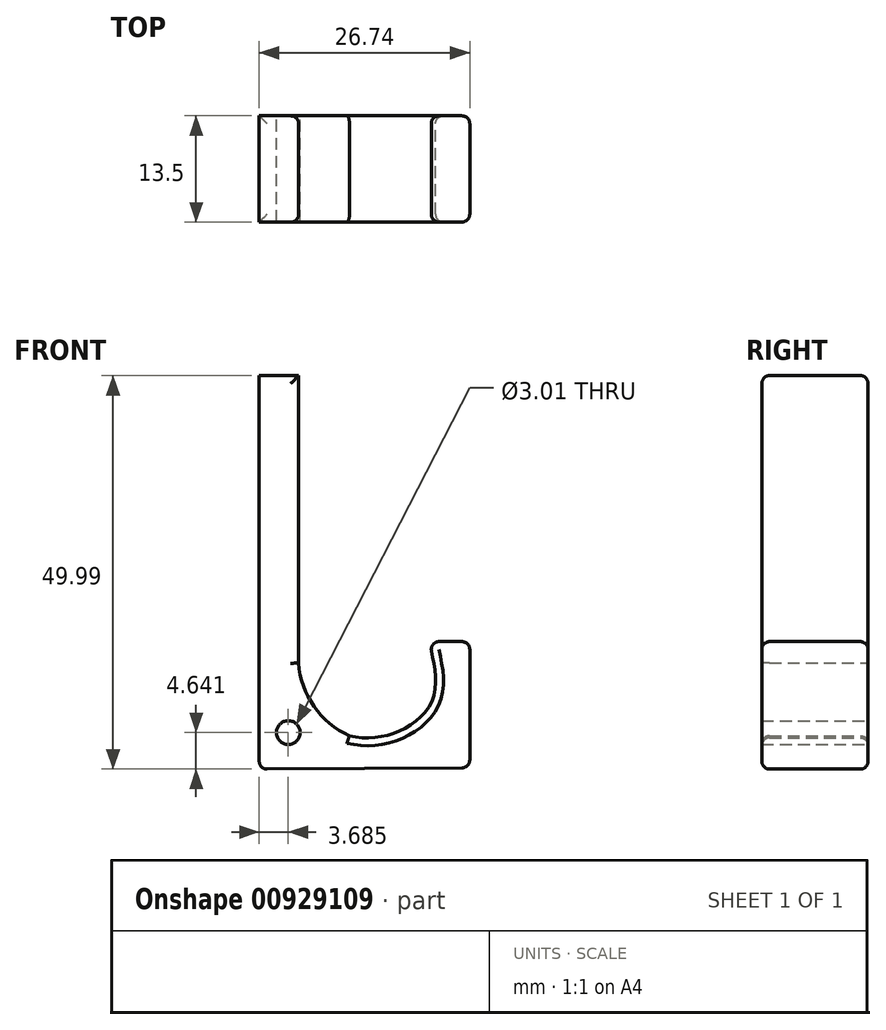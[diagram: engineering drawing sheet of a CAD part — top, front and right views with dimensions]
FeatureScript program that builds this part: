
annotation { "Feature Type Name" : "Feature", "Feature Type Description" : "" }
export const myFeature = defineFeature(function(context is Context, id is Id, definition is map)
    precondition{}
    {
        {
            var Q0;
            Q0=qCreatedBy(makeId("Front.planeOp"),FACE);
            var sketch = newSketch(context, id + "F0", { "sketchPlane" : qUnion([Q0])});
            skLineSegment(sketch, "E0", {"start": v(5.1, 13.49) * mm, "end": v(5.1, 50) * mm});
            skArc(sketch, "E1", {"start": v(5.1, 13.49) * mm, "mid": v(6.25, 9.3) * mm, "end": v(8.93, 5.9) * mm});
            skLineSegment(sketch, "E2.0", {"start": v(0.1, 0) * mm, "end": v(0.1, 50) * mm});
            skLineSegment(sketch, "E2.1", {"start": v(0.1, 0) * mm, "end": v(26.84, 0.17) * mm});
            skArc(sketch, "E3", {"start": v(5.1, 13.49) * mm, "mid": v(7.05, 7.97) * mm, "end": v(11.56, 4.24) * mm});
            skLineSegment(sketch, "E4", {"start": v(26.84, 16.2) * mm, "end": v(26.84, 0.17) * mm});
            skLineSegment(sketch, "E5", {"start": v(0.1, 50) * mm, "end": v(5.1, 50) * mm});
            skLineSegment(sketch, "E6", {"start": v(26.84, 16.2) * mm, "end": v(21.84, 16.2) * mm});
            skFitSpline(sketch, "E7", {"points": [v(21.84, 16.2) * mm, v(22.16, 8.97) * mm, v(11.56, 4.24) * mm], "startDerivative": vector(-0.62, -8.51) * mm, "endDerivative": vector(-24.07, 5.81) * mm});
            skCircle(sketch, "E8", {"center": v(3.79, 4.65) * mm, "radius": 1.5 * mm});
            skSolve(sketch);
        }
        {
            var Q0;
            {var subQ1=sQuery(id+"F0.wireOp",EDGE,"E0");Q0=makeQuery(id+"F0.imprint","IMPRINT",FACE,{"disambiguationData":[TD([[makeQuery(id+"F0.imprint","IMPRINT",EDGE,{"derivedFrom":subQ1}),1.0]])]});}
            extrude(context, id + "F1", {"entities" : qUnion([Q0]), "depth" : 13.5 * mm, "offsetDistance" : 25 * mm});
        }
        {
            var Q0;
            Q0=makeQuery(id+"F1.opExtrude","CAP_EDGE",EDGE,{"disambiguationData":[OSD([sQuery(id+"F0.wireOp",EDGE,"E7")])],"isStart":false});
            var Q1;
            Q1=makeQuery(id+"F1.opExtrude","CAP_EDGE",EDGE,{"disambiguationData":[OSD([sQuery(id+"F0.wireOp",EDGE,"E7")])],"isStart":true});
            var Q2;
            Q2=makeQuery(id+"F1.opExtrude","CAP_EDGE",EDGE,{"disambiguationData":[OSD([sQuery(id+"F0.wireOp",EDGE,"E4")])],"isStart":false});
            var Q3;
            Q3=makeQuery(id+"F1.opExtrude","CAP_EDGE",EDGE,{"disambiguationData":[OSD([sQuery(id+"F0.wireOp",EDGE,"E4")])],"isStart":true});
            var Q4;
            Q4=makeQuery(id+"F1.opExtrude","SWEPT_EDGE",EDGE,{"disambiguationData":[OSD([sQuery(id+"F0.wireOp",EDGE,"E2.1"),sQuery(id+"F0.wireOp",EDGE,"E4")])]});
            var Q5;
            Q5=makeQuery(id+"F1.opExtrude","SWEPT_EDGE",EDGE,{"disambiguationData":[OSD([sQuery(id+"F0.wireOp",EDGE,"E4"),sQuery(id+"F0.wireOp",EDGE,"E6")])]});
            var Q6;
            Q6=makeQuery(id+"F1.opExtrude","SWEPT_EDGE",EDGE,{"disambiguationData":[OSD([sQuery(id+"F0.wireOp",EDGE,"E6"),sQuery(id+"F0.wireOp",EDGE,"E7")])]});
            var Q7;
            Q7=makeQuery(id+"F1.opExtrude","CAP_EDGE",EDGE,{"disambiguationData":[OSD([sQuery(id+"F0.wireOp",EDGE,"E6")])],"isStart":false});
            var Q8;
            Q8=makeQuery(id+"F1.opExtrude","CAP_EDGE",EDGE,{"disambiguationData":[OSD([sQuery(id+"F0.wireOp",EDGE,"E6")])],"isStart":true});
            var Q9;
            Q9=makeQuery(id+"F1.opExtrude","CAP_EDGE",EDGE,{"disambiguationData":[OSD([sQuery(id+"F0.wireOp",EDGE,"E3")])],"isStart":true});
            var Q10;
            Q10=makeQuery(id+"F1.opExtrude","CAP_EDGE",EDGE,{"disambiguationData":[OSD([sQuery(id+"F0.wireOp",EDGE,"E0")])],"isStart":true});
            var Q11;
            Q11=makeQuery(id+"F1.opExtrude","CAP_EDGE",EDGE,{"disambiguationData":[OSD([sQuery(id+"F0.wireOp",EDGE,"E0")])],"isStart":false});
            var Q12;
            Q12=makeQuery(id+"F1.opExtrude","CAP_EDGE",EDGE,{"disambiguationData":[OSD([sQuery(id+"F0.wireOp",EDGE,"E2.1")])],"isStart":true});
            var Q13;
            Q13=makeQuery(id+"F1.opExtrude","CAP_EDGE",EDGE,{"disambiguationData":[OSD([sQuery(id+"F0.wireOp",EDGE,"E2.1")])],"isStart":false});
            var Q14;
            Q14=makeQuery(id+"F1.opExtrude","SWEPT_EDGE",EDGE,{"disambiguationData":[OSD([sQuery(id+"F0.wireOp",EDGE,"E2.0"),sQuery(id+"F0.wireOp",EDGE,"E2.1")])]});
            var Q15;
            Q15=makeQuery(id+"F1.opExtrude","CAP_EDGE",EDGE,{"disambiguationData":[OSD([sQuery(id+"F0.wireOp",EDGE,"E5")])],"isStart":false});
            var Q16;
            Q16=makeQuery(id+"F1.opExtrude","CAP_EDGE",EDGE,{"disambiguationData":[OSD([sQuery(id+"F0.wireOp",EDGE,"E5")])],"isStart":true});
            fillet(context, id + "F2", {"entities" : qUnion([Q0, Q1, Q2, Q3, Q4, Q5, Q6, Q7, Q8, Q9, Q10, Q11, Q12, Q13, Q14, Q15, Q16]), "radius" : 1 * mm, "tangentPropagation" : true, "allowEdgeOverflow" : false});
        }
    });
